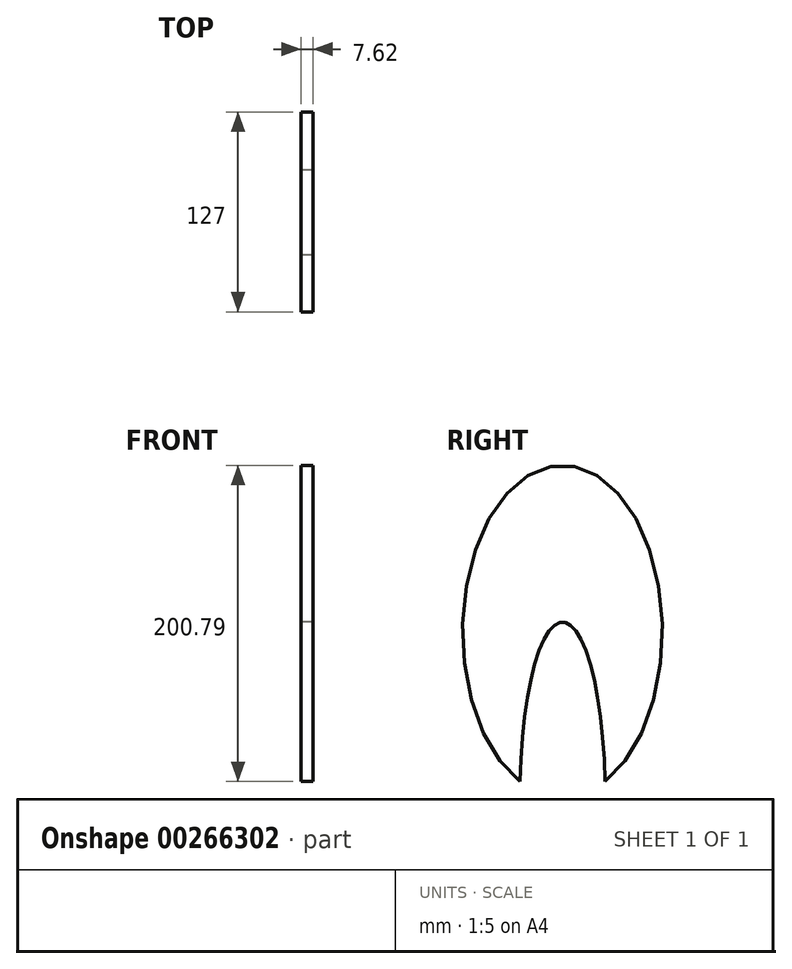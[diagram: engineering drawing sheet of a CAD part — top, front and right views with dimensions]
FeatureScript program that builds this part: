
annotation { "Feature Type Name" : "Feature", "Feature Type Description" : "" }
export const myFeature = defineFeature(function(context is Context, id is Id, definition is map)
    precondition{}
    {
        {
            var Q0;
            Q0=qCreatedBy(makeId("Right.planeOp"),FACE);
            var sketch = newSketch(context, id + "F0", { "sketchPlane" : qUnion([Q0])});
            skEllipse(sketch, "E0", {"center": v(0, 0) * mm, "majorRadius": 105.41 * mm, "minorRadius": 63.5 * mm, "majorAxis": v(0, 1)});
            skSolve(sketch);
        }
        {
            var Q0;
            Q0 = qSketchRegion(id + "F0", true);
            extrude(context, id + "F1", {"entities" : qUnion([Q0]), "depth" : 7.62 * mm});
        }
        {
            var Q0;
            Q0=makeQuery(id+"F1.opExtrude","CAP_FACE",FACE,{"disambiguationData":[OSD([sQuery(id+"F0.wireOp",EDGE,"E0")])],"isStart":false});
            var sketch = newSketch(context, id + "F2", { "sketchPlane" : qUnion([Q0])});
            skEllipse(sketch, "E1", {"center": v(0, -105.41) * mm, "majorRadius": 111.34 * mm, "minorRadius": 27.14 * mm, "majorAxis": v(0, 1)});
            skSolve(sketch);
        }
        {
            var Q0;
            Q0 = qSketchRegion(id + "F2", true);
            extrude(context, id + "F3", {"entities" : qUnion([Q0]), "operationType" : NewBodyOperationType.REMOVE, "oppositeDirection" : true, "depth" : 25.4 * mm});
        }
    });
